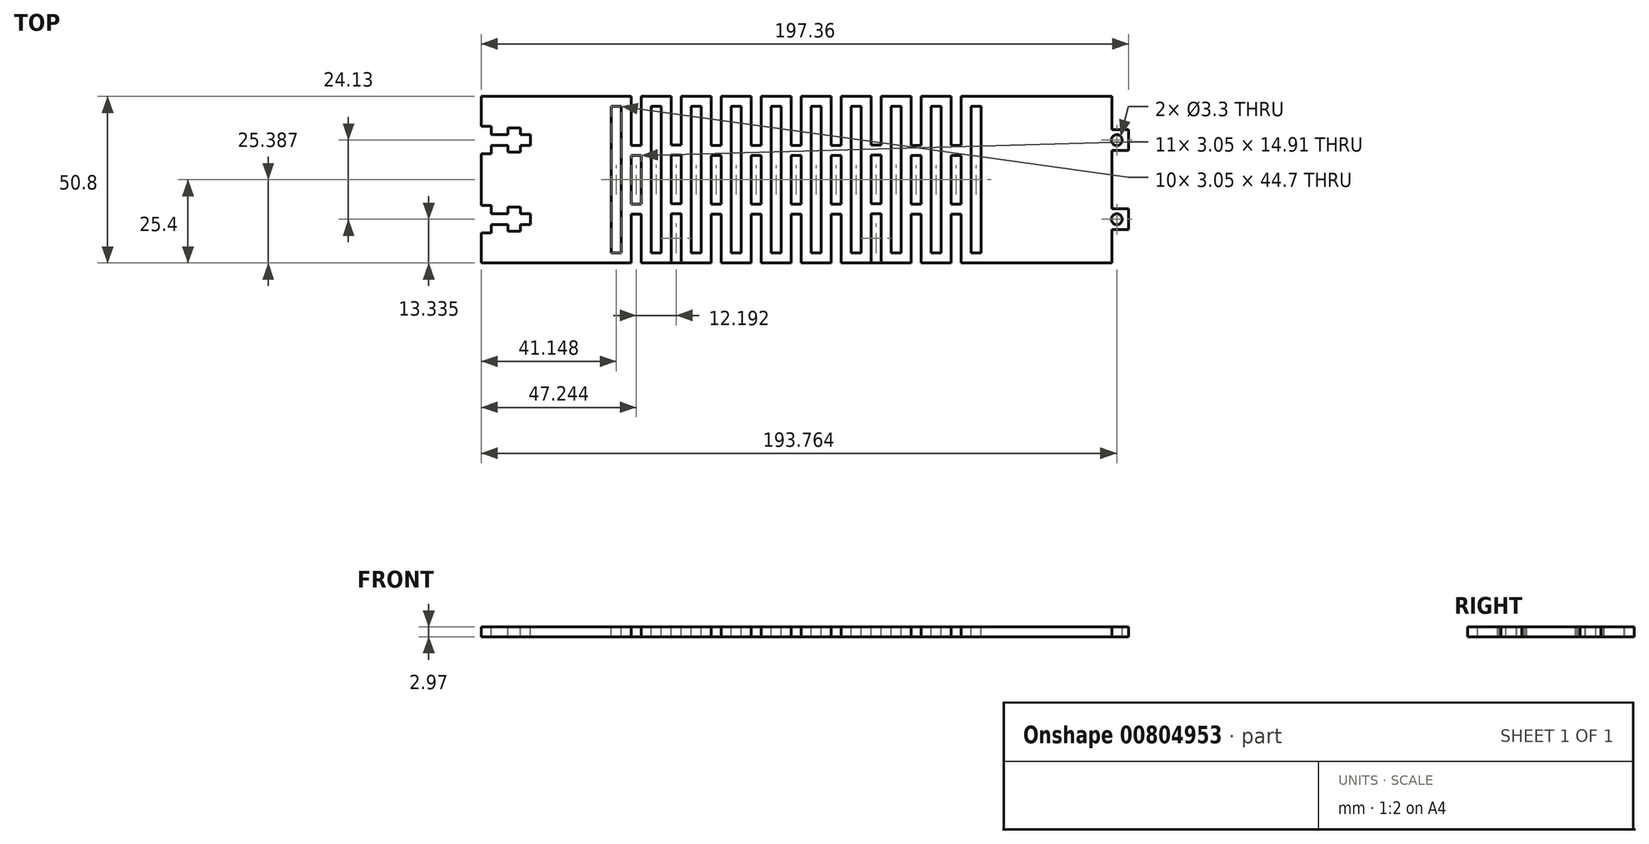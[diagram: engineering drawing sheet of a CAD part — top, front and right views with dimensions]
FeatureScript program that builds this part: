
annotation { "Feature Type Name" : "Feature", "Feature Type Description" : "" }
export const myFeature = defineFeature(function(context is Context, id is Id, definition is map)
    precondition{}
    {
        {
            var Q0;
            Q0=qCreatedBy(makeId("Top.planeOp"),FACE);
            var sketch = newSketch(context, id + "F0", { "sketchPlane" : qUnion([Q0])});
            skLineSegment(sketch, "E0.bottom", {"start": v(0, 0) * mm, "end": v(192.28, 0) * mm});
            skLineSegment(sketch, "E0.top", {"start": v(0, 50.8) * mm, "end": v(192.28, 50.8) * mm});
            skLineSegment(sketch, "E0.left", {"start": v(0, 0) * mm, "end": v(0, 50.8) * mm});
            skLineSegment(sketch, "E0.right", {"start": v(192.28, 0) * mm, "end": v(192.28, 50.8) * mm});
            skLineSegment(sketch, "E1.bottom", {"start": v(192.28, 40.64) * mm, "end": v(197.36, 40.64) * mm});
            skLineSegment(sketch, "E1.top", {"start": v(192.28, 34.3) * mm, "end": v(197.36, 34.3) * mm});
            skLineSegment(sketch, "E1.left", {"start": v(192.28, 40.64) * mm, "end": v(192.28, 34.3) * mm});
            skLineSegment(sketch, "E1.right", {"start": v(197.36, 40.64) * mm, "end": v(197.36, 34.3) * mm});
            skLineSegment(sketch, "E2.bottom", {"start": v(192.28, 16.51) * mm, "end": v(197.36, 16.51) * mm});
            skLineSegment(sketch, "E2.top", {"start": v(192.28, 10.16) * mm, "end": v(197.36, 10.16) * mm});
            skLineSegment(sketch, "E2.left", {"start": v(192.28, 16.51) * mm, "end": v(192.28, 10.16) * mm});
            skLineSegment(sketch, "E2.right", {"start": v(197.36, 16.51) * mm, "end": v(197.36, 10.16) * mm});
            skSolve(sketch);
        }
        {
            var Q0;
            Q0=makeQuery(id+"F0.imprint","IMPRINT",FACE,{"disambiguationData":[TD([[makeQuery(id+"F0.imprint","IMPRINT",EDGE,{"derivedFrom":sQuery(id+"F0.wireOp",EDGE,"E1.bottom")}),-1.0]])]});
            var Q1;
            Q1=makeQuery(id+"F0.imprint","IMPRINT",FACE,{"disambiguationData":[TD([[makeQuery(id+"F0.imprint","IMPRINT",EDGE,{"derivedFrom":sQuery(id+"F0.wireOp",EDGE,"E2.bottom")}),-1.0]])]});
            var Q2;
            {var subQ1=sQuery(id+"F0.wireOp",EDGE,"E0.bottom");Q2=makeQuery(id+"F0.imprint","IMPRINT",FACE,{"disambiguationData":[TD([[makeQuery(id+"F0.imprint","IMPRINT",EDGE,{"derivedFrom":subQ1}),1.0]])]});}
            extrude(context, id + "F1", {"entities" : qUnion([Q0, Q1, Q2]), "depth" : 2.97 * mm, "offsetDistance" : 25.4 * mm});
        }
        {
            var Q0;
            Q0=makeQuery(id+"F1.opExtrude","CAP_FACE",FACE,{"disambiguationData":[OSD([sQuery(id+"F0.wireOp",EDGE,"E0.bottom"),sQuery(id+"F0.wireOp",EDGE,"E0.top"),sQuery(id+"F0.wireOp",EDGE,"E0.left"),sQuery(id+"F0.wireOp",EDGE,"E0.right"),sQuery(id+"F0.wireOp",EDGE,"E1.bottom"),sQuery(id+"F0.wireOp",EDGE,"E1.top"),sQuery(id+"F0.wireOp",EDGE,"E1.right"),sQuery(id+"F0.wireOp",EDGE,"E2.bottom"),sQuery(id+"F0.wireOp",EDGE,"E2.top"),sQuery(id+"F0.wireOp",EDGE,"E2.right")])],"isStart":false});
            var sketch = newSketch(context, id + "F2", { "sketchPlane" : qUnion([Q0])});
            skCircle(sketch, "E3", {"center": v(193.76, 37.47) * mm, "radius": 1.65 * mm});
            skPoint(sketch, "E3.centerSnap0", {"position": v(197.36, 37.47) * mm});
            skCircle(sketch, "E4", {"center": v(193.76, 13.34) * mm, "radius": 1.65 * mm});
            skPoint(sketch, "E4.centerSnap0", {"position": v(197.36, 13.34) * mm});
            skLineSegment(sketch, "E5.bottom", {"start": v(0, 41.66) * mm, "end": v(3.05, 41.66) * mm});
            skLineSegment(sketch, "E5.top", {"start": v(0, 33.27) * mm, "end": v(3.05, 33.27) * mm});
            skLineSegment(sketch, "E5.left", {"start": v(0, 41.66) * mm, "end": v(0, 33.27) * mm});
            skLineSegment(sketch, "E5.right", {"start": v(3.05, 41.66) * mm, "end": v(3.05, 33.27) * mm});
            skLineSegment(sketch, "E6.bottom", {"start": v(3.05, 39.12) * mm, "end": v(8.13, 39.12) * mm});
            skLineSegment(sketch, "E6.top", {"start": v(3.05, 35.81) * mm, "end": v(8.13, 35.81) * mm});
            skLineSegment(sketch, "E6.left", {"start": v(3.05, 39.12) * mm, "end": v(3.05, 35.81) * mm});
            skLineSegment(sketch, "E6.right", {"start": v(8.13, 39.12) * mm, "end": v(8.13, 35.81) * mm});
            skLineSegment(sketch, "E7.bottom", {"start": v(8.13, 33.78) * mm, "end": v(11.94, 33.78) * mm});
            skLineSegment(sketch, "E7.top", {"start": v(8.13, 41.15) * mm, "end": v(11.94, 41.15) * mm});
            skLineSegment(sketch, "E7.left", {"start": v(8.13, 33.78) * mm, "end": v(8.13, 41.15) * mm});
            skLineSegment(sketch, "E7.right", {"start": v(11.94, 33.78) * mm, "end": v(11.94, 41.15) * mm});
            skLineSegment(sketch, "E8.bottom", {"start": v(11.94, 39.12) * mm, "end": v(14.99, 39.12) * mm});
            skLineSegment(sketch, "E8.top", {"start": v(11.94, 35.81) * mm, "end": v(14.99, 35.81) * mm});
            skLineSegment(sketch, "E8.left", {"start": v(11.94, 39.12) * mm, "end": v(11.94, 35.81) * mm});
            skLineSegment(sketch, "E8.right", {"start": v(14.99, 39.12) * mm, "end": v(14.99, 35.81) * mm});
            skLineSegment(sketch, "E9.bottom", {"start": v(0, 17.53) * mm, "end": v(3.05, 17.53) * mm});
            skLineSegment(sketch, "E9.top", {"start": v(0, 9.14) * mm, "end": v(3.05, 9.14) * mm});
            skLineSegment(sketch, "E9.left", {"start": v(0, 17.53) * mm, "end": v(0, 9.14) * mm});
            skLineSegment(sketch, "E9.right", {"start": v(3.05, 17.53) * mm, "end": v(3.05, 9.14) * mm});
            skLineSegment(sketch, "E10.bottom", {"start": v(3.05, 14.99) * mm, "end": v(8.13, 14.99) * mm});
            skLineSegment(sketch, "E10.top", {"start": v(3.05, 11.68) * mm, "end": v(8.13, 11.68) * mm});
            skLineSegment(sketch, "E10.left", {"start": v(3.05, 14.99) * mm, "end": v(3.05, 11.68) * mm});
            skLineSegment(sketch, "E10.right", {"start": v(8.13, 14.99) * mm, "end": v(8.13, 11.68) * mm});
            skLineSegment(sketch, "E11.bottom", {"start": v(8.13, 9.65) * mm, "end": v(11.94, 9.65) * mm});
            skLineSegment(sketch, "E11.top", {"start": v(8.13, 17.02) * mm, "end": v(11.94, 17.02) * mm});
            skLineSegment(sketch, "E11.left", {"start": v(8.13, 9.65) * mm, "end": v(8.13, 17.02) * mm});
            skLineSegment(sketch, "E11.right", {"start": v(11.94, 9.65) * mm, "end": v(11.94, 17.02) * mm});
            skLineSegment(sketch, "E12.bottom", {"start": v(11.94, 14.99) * mm, "end": v(14.99, 14.99) * mm});
            skLineSegment(sketch, "E12.top", {"start": v(11.94, 11.68) * mm, "end": v(14.99, 11.68) * mm});
            skLineSegment(sketch, "E12.left", {"start": v(11.94, 14.99) * mm, "end": v(11.94, 11.68) * mm});
            skLineSegment(sketch, "E12.right", {"start": v(14.99, 14.99) * mm, "end": v(14.99, 11.68) * mm});
            skLineSegment(sketch, "E13.bottom", {"start": v(76.2, 3.05) * mm, "end": v(79.25, 3.05) * mm});
            skLineSegment(sketch, "E13.top", {"start": v(76.2, 47.75) * mm, "end": v(79.25, 47.75) * mm});
            skLineSegment(sketch, "E13.left", {"start": v(76.2, 3.05) * mm, "end": v(76.2, 47.75) * mm});
            skLineSegment(sketch, "E13.right", {"start": v(79.25, 3.05) * mm, "end": v(79.25, 47.75) * mm});
            skLineSegment(sketch, "E14.bottom", {"start": v(82.3, 50.8) * mm, "end": v(85.34, 50.8) * mm});
            skLineSegment(sketch, "E14.top", {"start": v(82.3, 35.9) * mm, "end": v(85.34, 35.9) * mm});
            skLineSegment(sketch, "E14.left", {"start": v(82.3, 50.8) * mm, "end": v(82.3, 35.9) * mm});
            skLineSegment(sketch, "E14.right", {"start": v(85.34, 50.8) * mm, "end": v(85.34, 35.9) * mm});
            skLineSegment(sketch, "E15.bottom", {"start": v(82.3, 0) * mm, "end": v(85.34, 0) * mm});
            skLineSegment(sketch, "E15.top", {"start": v(82.3, 14.9) * mm, "end": v(85.34, 14.9) * mm});
            skLineSegment(sketch, "E15.left", {"start": v(82.3, 0) * mm, "end": v(82.3, 14.9) * mm});
            skLineSegment(sketch, "E15.right", {"start": v(85.34, 0) * mm, "end": v(85.34, 14.9) * mm});
            skLineSegment(sketch, "E16.bottom", {"start": v(82.3, 32.84) * mm, "end": v(85.34, 32.84) * mm});
            skLineSegment(sketch, "E16.top", {"start": v(82.3, 17.93) * mm, "end": v(85.34, 17.93) * mm});
            skLineSegment(sketch, "E16.left", {"start": v(82.3, 32.84) * mm, "end": v(82.3, 17.93) * mm});
            skLineSegment(sketch, "E16.right", {"start": v(85.34, 32.84) * mm, "end": v(85.34, 17.93) * mm});
            skLineSegment(sketch, "E17.bottom", {"start": v(88.4, 3.05) * mm, "end": v(91.44, 3.05) * mm});
            skLineSegment(sketch, "E17.top", {"start": v(88.4, 47.75) * mm, "end": v(91.44, 47.75) * mm});
            skLineSegment(sketch, "E17.left", {"start": v(88.4, 3.05) * mm, "end": v(88.4, 47.75) * mm});
            skLineSegment(sketch, "E17.right", {"start": v(91.44, 3.05) * mm, "end": v(91.44, 47.75) * mm});
            skLineSegment(sketch, "E18.bottom", {"start": v(94.49, 50.8) * mm, "end": v(97.54, 50.8) * mm});
            skLineSegment(sketch, "E18.top", {"start": v(94.49, 35.9) * mm, "end": v(97.54, 35.9) * mm});
            skLineSegment(sketch, "E18.left", {"start": v(94.49, 50.8) * mm, "end": v(94.49, 35.9) * mm});
            skLineSegment(sketch, "E18.right", {"start": v(97.54, 50.8) * mm, "end": v(97.54, 35.9) * mm});
            skLineSegment(sketch, "E19.bottom", {"start": v(94.49, 0) * mm, "end": v(97.54, 0) * mm});
            skLineSegment(sketch, "E19.top", {"start": v(94.49, 14.9) * mm, "end": v(97.54, 14.9) * mm});
            skLineSegment(sketch, "E19.left", {"start": v(94.49, 0) * mm, "end": v(94.49, 14.9) * mm});
            skLineSegment(sketch, "E19.right", {"start": v(97.54, 0) * mm, "end": v(97.54, 14.9) * mm});
            skLineSegment(sketch, "E20.bottom", {"start": v(94.49, 32.84) * mm, "end": v(97.54, 32.84) * mm});
            skLineSegment(sketch, "E20.top", {"start": v(94.49, 17.93) * mm, "end": v(97.54, 17.93) * mm});
            skLineSegment(sketch, "E20.left", {"start": v(94.49, 32.84) * mm, "end": v(94.49, 17.93) * mm});
            skLineSegment(sketch, "E20.right", {"start": v(97.54, 32.84) * mm, "end": v(97.54, 17.93) * mm});
            skLineSegment(sketch, "E21.bottom", {"start": v(100.58, 3.05) * mm, "end": v(103.63, 3.05) * mm});
            skLineSegment(sketch, "E21.top", {"start": v(100.58, 47.75) * mm, "end": v(103.63, 47.75) * mm});
            skLineSegment(sketch, "E21.left", {"start": v(100.58, 3.05) * mm, "end": v(100.58, 47.75) * mm});
            skLineSegment(sketch, "E21.right", {"start": v(103.63, 3.05) * mm, "end": v(103.63, 47.75) * mm});
            skLineSegment(sketch, "E22.bottom", {"start": v(106.68, 50.8) * mm, "end": v(109.73, 50.8) * mm});
            skLineSegment(sketch, "E22.top", {"start": v(106.68, 35.9) * mm, "end": v(109.73, 35.9) * mm});
            skLineSegment(sketch, "E22.left", {"start": v(106.68, 50.8) * mm, "end": v(106.68, 35.9) * mm});
            skLineSegment(sketch, "E22.right", {"start": v(109.73, 50.8) * mm, "end": v(109.73, 35.9) * mm});
            skLineSegment(sketch, "E23.bottom", {"start": v(106.68, 0) * mm, "end": v(109.73, 0) * mm});
            skLineSegment(sketch, "E23.top", {"start": v(106.68, 14.9) * mm, "end": v(109.73, 14.9) * mm});
            skLineSegment(sketch, "E23.left", {"start": v(106.68, 0) * mm, "end": v(106.68, 14.9) * mm});
            skLineSegment(sketch, "E23.right", {"start": v(109.73, 0) * mm, "end": v(109.73, 14.9) * mm});
            skLineSegment(sketch, "E24.bottom", {"start": v(106.68, 32.84) * mm, "end": v(109.73, 32.84) * mm});
            skLineSegment(sketch, "E24.top", {"start": v(106.68, 17.93) * mm, "end": v(109.73, 17.93) * mm});
            skLineSegment(sketch, "E24.left", {"start": v(106.68, 32.84) * mm, "end": v(106.68, 17.93) * mm});
            skLineSegment(sketch, "E24.right", {"start": v(109.73, 32.84) * mm, "end": v(109.73, 17.93) * mm});
            skLineSegment(sketch, "E25.bottom", {"start": v(112.78, 3.05) * mm, "end": v(115.82, 3.05) * mm});
            skLineSegment(sketch, "E25.top", {"start": v(112.78, 47.75) * mm, "end": v(115.82, 47.75) * mm});
            skLineSegment(sketch, "E25.left", {"start": v(112.78, 3.05) * mm, "end": v(112.78, 47.75) * mm});
            skLineSegment(sketch, "E25.right", {"start": v(115.82, 3.05) * mm, "end": v(115.82, 47.75) * mm});
            skLineSegment(sketch, "E26.bottom", {"start": v(64, 3.05) * mm, "end": v(67.06, 3.05) * mm});
            skLineSegment(sketch, "E26.top", {"start": v(64, 47.75) * mm, "end": v(67.06, 47.75) * mm});
            skLineSegment(sketch, "E26.left", {"start": v(64, 3.05) * mm, "end": v(64, 47.75) * mm});
            skLineSegment(sketch, "E26.right", {"start": v(67.06, 3.05) * mm, "end": v(67.06, 47.75) * mm});
            skLineSegment(sketch, "E27.bottom", {"start": v(70.1, 50.8) * mm, "end": v(73.15, 50.8) * mm});
            skLineSegment(sketch, "E27.top", {"start": v(70.1, 35.9) * mm, "end": v(73.15, 35.9) * mm});
            skLineSegment(sketch, "E27.left", {"start": v(70.1, 50.8) * mm, "end": v(70.1, 35.9) * mm});
            skLineSegment(sketch, "E27.right", {"start": v(73.15, 50.8) * mm, "end": v(73.15, 35.9) * mm});
            skLineSegment(sketch, "E28.bottom", {"start": v(70.1, 0) * mm, "end": v(73.15, 0) * mm});
            skLineSegment(sketch, "E28.top", {"start": v(70.1, 14.9) * mm, "end": v(73.15, 14.9) * mm});
            skLineSegment(sketch, "E28.left", {"start": v(70.1, 0) * mm, "end": v(70.1, 14.9) * mm});
            skLineSegment(sketch, "E28.right", {"start": v(73.15, 0) * mm, "end": v(73.15, 14.9) * mm});
            skLineSegment(sketch, "E29.bottom", {"start": v(70.1, 32.84) * mm, "end": v(73.15, 32.84) * mm});
            skLineSegment(sketch, "E29.top", {"start": v(70.1, 17.93) * mm, "end": v(73.15, 17.93) * mm});
            skLineSegment(sketch, "E29.left", {"start": v(70.1, 32.84) * mm, "end": v(70.1, 17.93) * mm});
            skLineSegment(sketch, "E29.right", {"start": v(73.15, 32.84) * mm, "end": v(73.15, 17.93) * mm});
            skLineSegment(sketch, "E30.bottom", {"start": v(118.87, 50.88) * mm, "end": v(121.92, 50.88) * mm});
            skLineSegment(sketch, "E30.top", {"start": v(118.87, 35.97) * mm, "end": v(121.92, 35.97) * mm});
            skLineSegment(sketch, "E30.left", {"start": v(118.87, 50.88) * mm, "end": v(118.87, 35.97) * mm});
            skLineSegment(sketch, "E30.right", {"start": v(121.92, 50.88) * mm, "end": v(121.92, 35.97) * mm});
            skLineSegment(sketch, "E31.bottom", {"start": v(118.87, 0.08) * mm, "end": v(121.92, 0.08) * mm});
            skLineSegment(sketch, "E31.top", {"start": v(118.87, 14.99) * mm, "end": v(121.92, 14.99) * mm});
            skLineSegment(sketch, "E31.left", {"start": v(118.87, 0.08) * mm, "end": v(118.87, 14.99) * mm});
            skLineSegment(sketch, "E31.right", {"start": v(121.92, 0.08) * mm, "end": v(121.92, 14.99) * mm});
            skLineSegment(sketch, "E32.bottom", {"start": v(118.87, 32.92) * mm, "end": v(121.92, 32.92) * mm});
            skLineSegment(sketch, "E32.top", {"start": v(118.87, 18) * mm, "end": v(121.92, 18) * mm});
            skLineSegment(sketch, "E32.left", {"start": v(118.87, 32.92) * mm, "end": v(118.87, 18) * mm});
            skLineSegment(sketch, "E32.right", {"start": v(121.92, 32.92) * mm, "end": v(121.92, 18) * mm});
            skLineSegment(sketch, "E33.bottom", {"start": v(124.97, 3.12) * mm, "end": v(128.02, 3.12) * mm});
            skLineSegment(sketch, "E33.top", {"start": v(124.97, 47.83) * mm, "end": v(128.02, 47.83) * mm});
            skLineSegment(sketch, "E33.left", {"start": v(124.97, 3.12) * mm, "end": v(124.97, 47.83) * mm});
            skLineSegment(sketch, "E33.right", {"start": v(128.02, 3.12) * mm, "end": v(128.02, 47.83) * mm});
            skLineSegment(sketch, "E34.bottom", {"start": v(51.82, 3.12) * mm, "end": v(54.86, 3.12) * mm});
            skLineSegment(sketch, "E34.top", {"start": v(51.82, 47.83) * mm, "end": v(54.86, 47.83) * mm});
            skLineSegment(sketch, "E34.left", {"start": v(51.82, 3.12) * mm, "end": v(51.82, 47.83) * mm});
            skLineSegment(sketch, "E34.right", {"start": v(54.86, 3.12) * mm, "end": v(54.86, 47.83) * mm});
            skLineSegment(sketch, "E35.bottom", {"start": v(57.91, 50.88) * mm, "end": v(60.96, 50.88) * mm});
            skLineSegment(sketch, "E35.top", {"start": v(57.91, 35.97) * mm, "end": v(60.96, 35.97) * mm});
            skLineSegment(sketch, "E35.left", {"start": v(57.91, 50.88) * mm, "end": v(57.91, 35.97) * mm});
            skLineSegment(sketch, "E35.right", {"start": v(60.96, 50.88) * mm, "end": v(60.96, 35.97) * mm});
            skLineSegment(sketch, "E36.bottom", {"start": v(57.91, 0.08) * mm, "end": v(60.96, 0.08) * mm});
            skLineSegment(sketch, "E36.top", {"start": v(57.91, 14.99) * mm, "end": v(60.96, 14.99) * mm});
            skLineSegment(sketch, "E36.left", {"start": v(57.91, 0.08) * mm, "end": v(57.91, 14.99) * mm});
            skLineSegment(sketch, "E36.right", {"start": v(60.96, 0.08) * mm, "end": v(60.96, 14.99) * mm});
            skLineSegment(sketch, "E37.bottom", {"start": v(57.91, 32.92) * mm, "end": v(60.96, 32.92) * mm});
            skLineSegment(sketch, "E37.top", {"start": v(57.91, 18) * mm, "end": v(60.96, 18) * mm});
            skLineSegment(sketch, "E37.left", {"start": v(57.91, 32.92) * mm, "end": v(57.91, 18) * mm});
            skLineSegment(sketch, "E37.right", {"start": v(60.96, 32.92) * mm, "end": v(60.96, 18) * mm});
            skLineSegment(sketch, "E38.bottom", {"start": v(131.06, 50.8) * mm, "end": v(134.11, 50.8) * mm});
            skLineSegment(sketch, "E38.top", {"start": v(131.06, 35.9) * mm, "end": v(134.11, 35.9) * mm});
            skLineSegment(sketch, "E38.left", {"start": v(131.06, 50.8) * mm, "end": v(131.06, 35.9) * mm});
            skLineSegment(sketch, "E38.right", {"start": v(134.11, 50.8) * mm, "end": v(134.11, 35.9) * mm});
            skLineSegment(sketch, "E39.bottom", {"start": v(131.06, 0) * mm, "end": v(134.11, 0) * mm});
            skLineSegment(sketch, "E39.top", {"start": v(131.06, 14.9) * mm, "end": v(134.11, 14.9) * mm});
            skLineSegment(sketch, "E39.left", {"start": v(131.06, 0) * mm, "end": v(131.06, 14.9) * mm});
            skLineSegment(sketch, "E39.right", {"start": v(134.11, 0) * mm, "end": v(134.11, 14.9) * mm});
            skLineSegment(sketch, "E40.bottom", {"start": v(131.06, 32.84) * mm, "end": v(134.11, 32.84) * mm});
            skLineSegment(sketch, "E40.top", {"start": v(131.06, 17.93) * mm, "end": v(134.11, 17.93) * mm});
            skLineSegment(sketch, "E40.left", {"start": v(131.06, 32.84) * mm, "end": v(131.06, 17.93) * mm});
            skLineSegment(sketch, "E40.right", {"start": v(134.11, 32.84) * mm, "end": v(134.11, 17.93) * mm});
            skLineSegment(sketch, "E41.bottom", {"start": v(137.16, 3.05) * mm, "end": v(140.2, 3.05) * mm});
            skLineSegment(sketch, "E41.top", {"start": v(137.16, 47.75) * mm, "end": v(140.2, 47.75) * mm});
            skLineSegment(sketch, "E41.left", {"start": v(137.16, 3.05) * mm, "end": v(137.16, 47.75) * mm});
            skLineSegment(sketch, "E41.right", {"start": v(140.2, 3.05) * mm, "end": v(140.2, 47.75) * mm});
            skLineSegment(sketch, "E42.bottom", {"start": v(39.62, 3.05) * mm, "end": v(42.67, 3.05) * mm});
            skLineSegment(sketch, "E42.top", {"start": v(39.62, 47.75) * mm, "end": v(42.67, 47.75) * mm});
            skLineSegment(sketch, "E42.left", {"start": v(39.62, 3.05) * mm, "end": v(39.62, 47.75) * mm});
            skLineSegment(sketch, "E42.right", {"start": v(42.67, 3.05) * mm, "end": v(42.67, 47.75) * mm});
            skLineSegment(sketch, "E43.bottom", {"start": v(45.72, 50.8) * mm, "end": v(48.77, 50.8) * mm});
            skLineSegment(sketch, "E43.top", {"start": v(45.72, 35.9) * mm, "end": v(48.77, 35.9) * mm});
            skLineSegment(sketch, "E43.left", {"start": v(45.72, 50.8) * mm, "end": v(45.72, 35.9) * mm});
            skLineSegment(sketch, "E43.right", {"start": v(48.77, 50.8) * mm, "end": v(48.77, 35.9) * mm});
            skLineSegment(sketch, "E44.bottom", {"start": v(45.72, 0) * mm, "end": v(48.77, 0) * mm});
            skLineSegment(sketch, "E44.top", {"start": v(45.72, 14.9) * mm, "end": v(48.77, 14.9) * mm});
            skLineSegment(sketch, "E44.left", {"start": v(45.72, 0) * mm, "end": v(45.72, 14.9) * mm});
            skLineSegment(sketch, "E44.right", {"start": v(48.77, 0) * mm, "end": v(48.77, 14.9) * mm});
            skLineSegment(sketch, "E45.left", {"start": v(45.72, 32.84) * mm, "end": v(45.72, 17.93) * mm});
            skLineSegment(sketch, "E45.right", {"start": v(51.82, 32.84) * mm, "end": v(51.82, 17.93) * mm});
            skLineSegment(sketch, "E46.bottom", {"start": v(143.26, 50.8) * mm, "end": v(146.3, 50.8) * mm});
            skLineSegment(sketch, "E46.top", {"start": v(143.26, 35.9) * mm, "end": v(146.3, 35.9) * mm});
            skLineSegment(sketch, "E46.left", {"start": v(143.26, 50.8) * mm, "end": v(143.26, 35.9) * mm});
            skLineSegment(sketch, "E46.right", {"start": v(146.3, 50.8) * mm, "end": v(146.3, 35.9) * mm});
            skLineSegment(sketch, "E47.bottom", {"start": v(143.26, 0) * mm, "end": v(146.3, 0) * mm});
            skLineSegment(sketch, "E47.top", {"start": v(143.26, 14.9) * mm, "end": v(146.3, 14.9) * mm});
            skLineSegment(sketch, "E47.left", {"start": v(143.26, 0) * mm, "end": v(143.26, 14.9) * mm});
            skLineSegment(sketch, "E47.right", {"start": v(146.3, 0) * mm, "end": v(146.3, 14.9) * mm});
            skLineSegment(sketch, "E48.bottom", {"start": v(143.26, 32.84) * mm, "end": v(146.3, 32.84) * mm});
            skLineSegment(sketch, "E48.top", {"start": v(143.26, 17.93) * mm, "end": v(146.3, 17.93) * mm});
            skLineSegment(sketch, "E48.left", {"start": v(143.26, 32.84) * mm, "end": v(143.26, 17.93) * mm});
            skLineSegment(sketch, "E48.right", {"start": v(146.3, 32.84) * mm, "end": v(146.3, 17.93) * mm});
            skLineSegment(sketch, "E49.bottom", {"start": v(149.35, 3.05) * mm, "end": v(152.4, 3.05) * mm});
            skLineSegment(sketch, "E49.top", {"start": v(149.35, 47.75) * mm, "end": v(152.4, 47.75) * mm});
            skLineSegment(sketch, "E49.left", {"start": v(149.35, 3.05) * mm, "end": v(149.35, 47.75) * mm});
            skLineSegment(sketch, "E49.right", {"start": v(152.4, 3.05) * mm, "end": v(152.4, 47.75) * mm});
            skLineSegment(sketch, "E50", {"start": v(45.72, 32.84) * mm, "end": v(48.77, 32.84) * mm});
            skLineSegment(sketch, "E51", {"start": v(48.77, 32.84) * mm, "end": v(48.77, 17.93) * mm});
            skLineSegment(sketch, "E52", {"start": v(48.77, 17.93) * mm, "end": v(45.72, 17.93) * mm});
            skSolve(sketch);
        }
        {
            var Q0;
            Q0=makeQuery(id+"F2.imprint","IMPRINT",FACE,{"disambiguationData":[TD([[makeQuery(id+"F2.imprint","IMPRINT",EDGE,{"derivedFrom":sQuery(id+"F2.wireOp",EDGE,"E3")}),-1.0]])]});
            var Q1;
            Q1=sQuery(id+"F2.wireOp",EDGE,"E3");
            var Q2;
            Q2=sQuery(id+"F2.wireOp",EDGE,"E4");
            extrude(context, id + "F3", {"entities" : qUnion([Q0]), "operationType" : NewBodyOperationType.INTERSECT, "surfaceEntities" : qUnion([Q1, Q2]), "oppositeDirection" : true, "depth" : 25.4 * mm, "offsetDistance" : 25.4 * mm});
        }
    });
